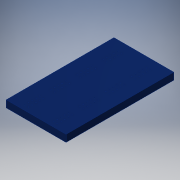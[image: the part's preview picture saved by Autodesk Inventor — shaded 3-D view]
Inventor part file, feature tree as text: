
AUTODESK INVENTOR PART (.ipt)
format: ipt  version: 2019.4 (Build 234330000, 330)  size: 399,360 bytes
history: native  units: in
note: dims shown in document units (in); Inventor stores cm internally (conversion verified against a paired STEP export)
features: extrude x4, sketch x4
ambient origin geometry x8: Origin, YZ Plane, XZ Plane, XY Plane, X Axis, Y Axis, Z Axis, Center Point
bodies: Solid1 (feature_tree)
feature tree (8):
  extrude  "Extrusion1"  Depth=8.5039in
  extrude  "Extrusion3"  Depth=0.5512in
  extrude  "Extrusion4"  Depth=0.3917in
  extrude  "Extrusion5"  Depth=0.1969in
  sketch  "Sketch1"  dims[d0=4.7244in d1=8.5039in]
  sketch  "Sketch4"  dims[d2=0.5512in d3=0.0in d31=0.0591in]
  sketch  "Sketch5"  dims[d32=1.0799in d33=0.3917in]
  sketch  "Sketch6"  dims[d34=1.9685in d36=0.2925in d37=0.7874in d39=0.2925in d42=1.5748in d44=2.0551in d45=0.7874in d47=2.272in d50=0.0in d51=0.0in d52=0.1575in d53=1.9685in d55=0.2925in d56=0.7874in d58=0.2925in d61=1.5748in d63=2.0551in d64=0.7874in d66=2.272in d69=0.4724in d70=0.0in d71=0.2953in d72=0.2953in d73=0.3937in d74=0.1969in d75=0.0in]
